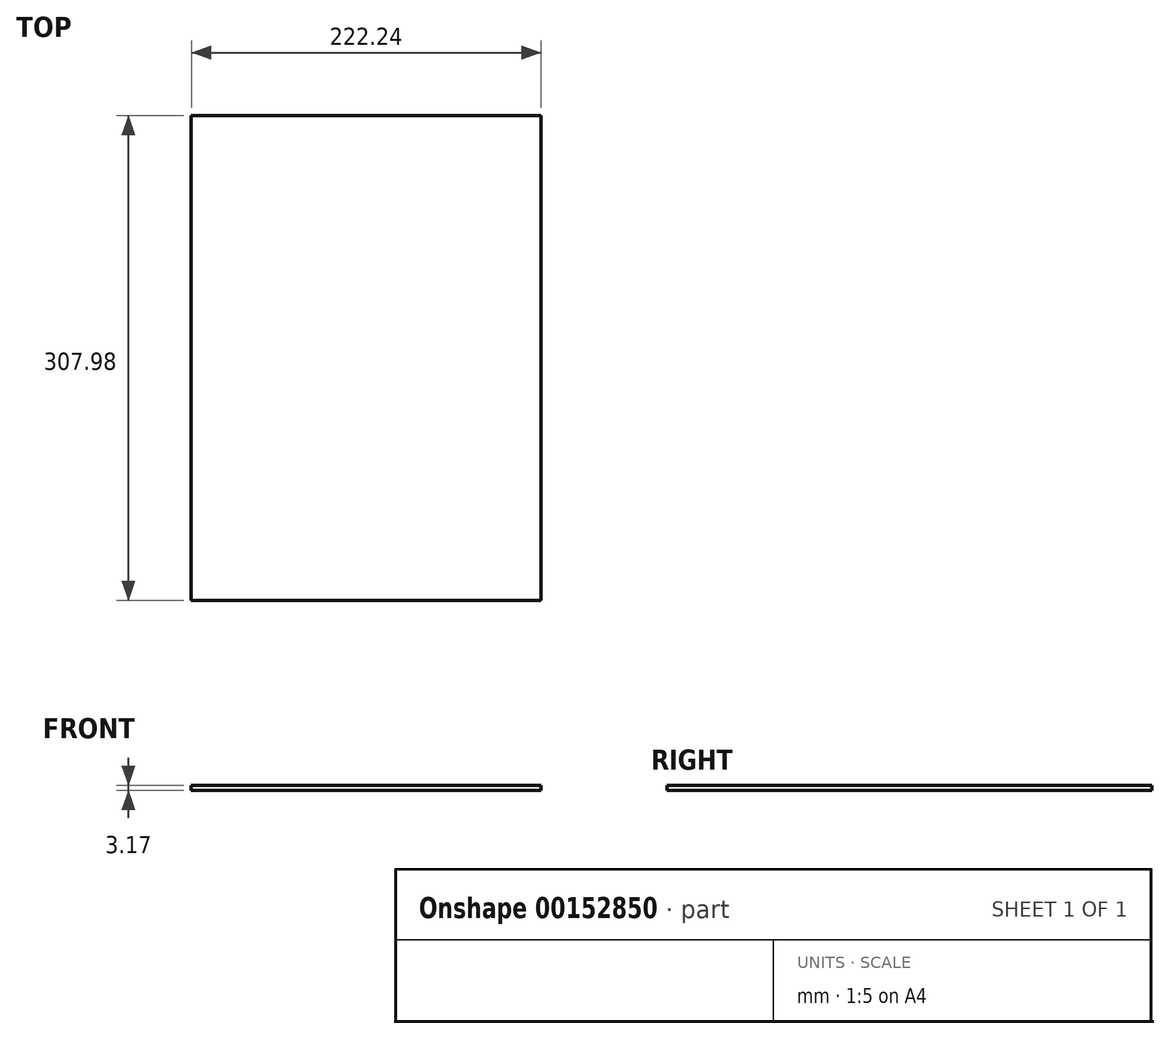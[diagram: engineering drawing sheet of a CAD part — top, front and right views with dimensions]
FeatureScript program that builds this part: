
annotation { "Feature Type Name" : "Feature", "Feature Type Description" : "" }
export const myFeature = defineFeature(function(context is Context, id is Id, definition is map)
    precondition{}
    {
        {
            var Q0;
            Q0=qCreatedBy(makeId("Top.planeOp"),FACE);
            var sketch = newSketch(context, id + "F0", { "sketchPlane" : qUnion([Q0])});
            skLineSegment(sketch, "E0.bottom", {"start": v(111.13, -153.99) * mm, "end": v(-111.13, -153.99) * mm});
            skLineSegment(sketch, "E0.top", {"start": v(111.13, 153.99) * mm, "end": v(-111.12, 153.99) * mm});
            skLineSegment(sketch, "E0.left", {"start": v(111.13, -153.99) * mm, "end": v(111.13, 153.99) * mm});
            skLineSegment(sketch, "E0.right", {"start": v(-111.13, -153.99) * mm, "end": v(-111.12, 153.99) * mm});
            skPoint(sketch, "E0.middle", {"position": v(0, 0) * mm});
            skSolve(sketch);
        }
        {
            var Q0;
            Q0 = qSketchRegion(id + "F0", true);
            extrude(context, id + "F1", {"entities" : qUnion([Q0]), "depth" : 3.17 * mm});
        }
    });
